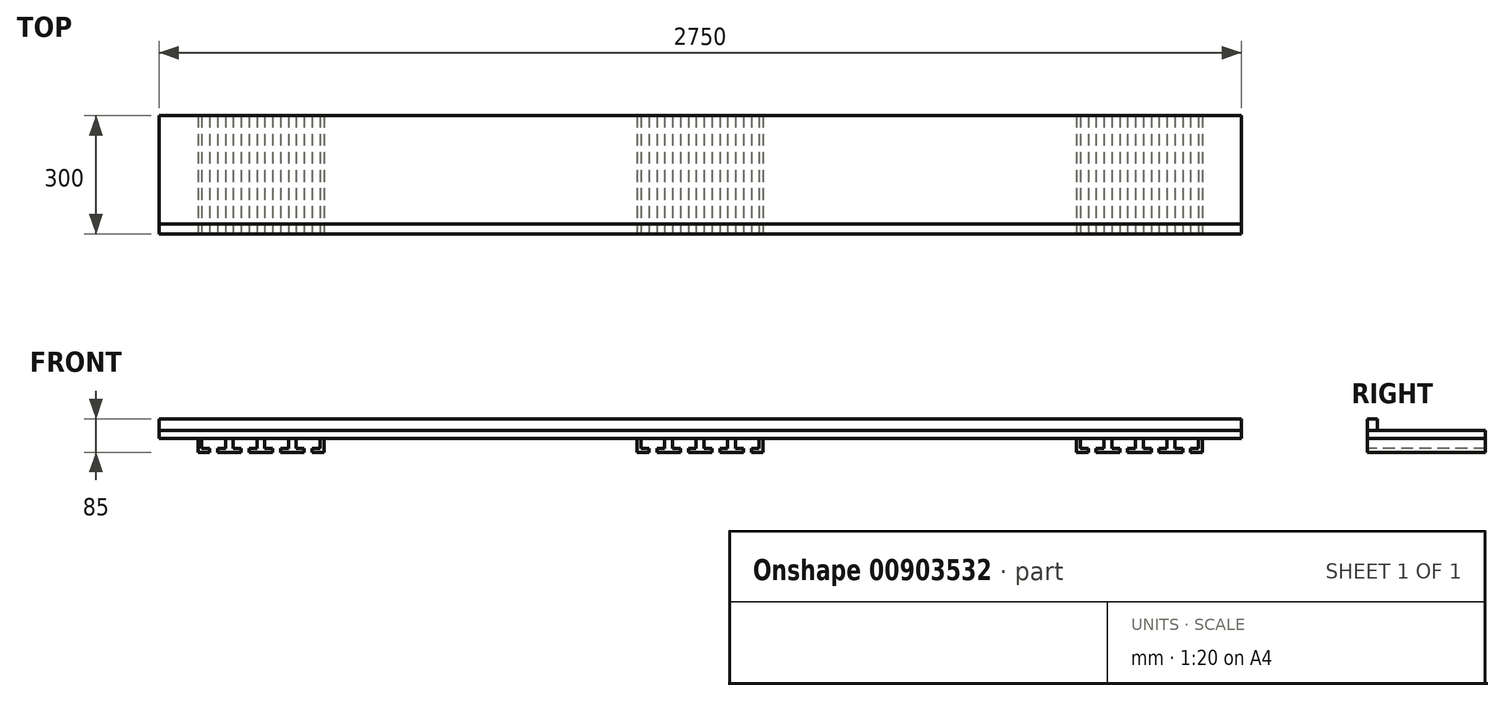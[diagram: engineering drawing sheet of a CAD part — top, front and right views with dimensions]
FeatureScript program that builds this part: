
annotation { "Feature Type Name" : "Feature", "Feature Type Description" : "" }
export const myFeature = defineFeature(function(context is Context, id is Id, definition is map)
    precondition{}
    {
        {
            var Q0;
            Q0=qCreatedBy(makeId("Front.planeOp"),FACE);
            var sketch = newSketch(context, id + "F0", { "sketchPlane" : qUnion([Q0])});
            skLineSegment(sketch, "E0.bottom", {"start": v(1375, -10) * mm, "end": v(-1375, -10) * mm});
            skLineSegment(sketch, "E0.top", {"start": v(1375, 10) * mm, "end": v(-1375, 10) * mm});
            skLineSegment(sketch, "E0.left", {"start": v(1375, -10) * mm, "end": v(1375, 10) * mm});
            skLineSegment(sketch, "E0.right", {"start": v(-1375, -10) * mm, "end": v(-1375, 10) * mm});
            skPoint(sketch, "E0.middle", {"position": v(0, 0) * mm});
            skSolve(sketch);
        }
        {
            var Q0;
            Q0 = qSketchRegion(id + "F0", true);
            extrude(context, id + "F1", {"entities" : qUnion([Q0]), "depth" : 300 * mm, "offsetDistance" : 25 * mm});
        }
        {
            var Q0;
            Q0=makeQuery(id+"F1.opExtrude","SWEPT_FACE",FACE,{"disambiguationData":[OSD([sQuery(id+"F0.wireOp",EDGE,"E0.top")])]});
            var sketch = newSketch(context, id + "F2", { "sketchPlane" : qUnion([Q0])});
            skLineSegment(sketch, "E1.bottom", {"start": v(-1375, -300) * mm, "end": v(1375, -300) * mm});
            skLineSegment(sketch, "E1.top", {"start": v(-1375, -275) * mm, "end": v(1375, -275) * mm});
            skLineSegment(sketch, "E1.left", {"start": v(-1375, -300) * mm, "end": v(-1375, -275) * mm});
            skLineSegment(sketch, "E1.right", {"start": v(1375, -300) * mm, "end": v(1375, -275) * mm});
            skSolve(sketch);
        }
        {
            var Q0;
            Q0 = qSketchRegion(id + "F2", true);
            extrude(context, id + "F3", {"entities" : qUnion([Q0]), "depth" : 30 * mm, "offsetDistance" : 25 * mm});
        }
        {
            var Q0;
            Q0=makeQuery(id+"F1.opExtrude","CAP_FACE",FACE,{"disambiguationData":[OSD([sQuery(id+"F0.wireOp",EDGE,"E0.bottom"),sQuery(id+"F0.wireOp",EDGE,"E0.top"),sQuery(id+"F0.wireOp",EDGE,"E0.left"),sQuery(id+"F0.wireOp",EDGE,"E0.right")])],"isStart":false});
            var sketch = newSketch(context, id + "F4", { "sketchPlane" : qUnion([Q0])});
            skLineSegment(sketch, "E2", {"start": v(0, 0) * mm, "end": v(0, -360.98) * mm, "construction": true});
            skLineSegment(sketch, "E3", {"start": v(0, 0) * mm, "end": v(0, -45) * mm});
            skLineSegment(sketch, "E4", {"start": v(0, -45) * mm, "end": v(30, -45) * mm});
            skLineSegment(sketch, "E5", {"start": v(30, -45) * mm, "end": v(30, -35) * mm});
            skLineSegment(sketch, "E6", {"start": v(30, -35) * mm, "end": v(10, -35) * mm});
            skLineSegment(sketch, "E7", {"start": v(10, -35) * mm, "end": v(10, -10) * mm});
            skLineSegment(sketch, "E8", {"start": v(10, -10) * mm, "end": v(0, -10) * mm});
            skLineSegment(sketch, "E9.MirrorCS", {"start": v(-10, -10) * mm, "end": v(0, -10) * mm});
            skLineSegment(sketch, "E10.MirrorCS", {"start": v(-10, -35) * mm, "end": v(-10, -10) * mm});
            skLineSegment(sketch, "E11.MirrorCS", {"start": v(-30, -35) * mm, "end": v(-10, -35) * mm});
            skLineSegment(sketch, "E12.MirrorCS", {"start": v(-30, -45) * mm, "end": v(-30, -35) * mm});
            skLineSegment(sketch, "E13.MirrorCS", {"start": v(0, -45) * mm, "end": v(-30, -45) * mm});
            skLineSegment(sketch, "E14", {"start": v(40, -10) * mm, "end": v(40, -247.73) * mm, "construction": true});
            skLineSegment(sketch, "E15.MirrorCS", {"start": v(80, -45) * mm, "end": v(50, -45) * mm});
            skLineSegment(sketch, "E16.MirrorCS", {"start": v(50, -45) * mm, "end": v(50, -35) * mm});
            skLineSegment(sketch, "E17.MirrorCS", {"start": v(50, -35) * mm, "end": v(70, -35) * mm});
            skLineSegment(sketch, "E18.MirrorCS", {"start": v(70, -35) * mm, "end": v(70, -10) * mm});
            skLineSegment(sketch, "E19.MirrorCS", {"start": v(70, -10) * mm, "end": v(80, -10) * mm});
            skLineSegment(sketch, "E20", {"start": v(80, -10) * mm, "end": v(80, -45) * mm});
            skLineSegment(sketch, "E21.MirrorCS", {"start": v(-80, -10) * mm, "end": v(-80, -45) * mm});
            skLineSegment(sketch, "E22.MirrorCS", {"start": v(-70, -10) * mm, "end": v(-80, -10) * mm});
            skLineSegment(sketch, "E23.MirrorCS", {"start": v(-70, -35) * mm, "end": v(-70, -10) * mm});
            skLineSegment(sketch, "E24.MirrorCS", {"start": v(-50, -35) * mm, "end": v(-70, -35) * mm});
            skLineSegment(sketch, "E25.MirrorCS", {"start": v(-50, -45) * mm, "end": v(-50, -35) * mm});
            skLineSegment(sketch, "E26.MirrorCS", {"start": v(-80, -45) * mm, "end": v(-50, -45) * mm});
            skLineSegment(sketch, "E27.MirrorCS", {"start": v(90, -10) * mm, "end": v(80, -10) * mm});
            skLineSegment(sketch, "E28.MirrorCS", {"start": v(90, -35) * mm, "end": v(90, -10) * mm});
            skLineSegment(sketch, "E29.MirrorCS", {"start": v(110, -35) * mm, "end": v(90, -35) * mm});
            skLineSegment(sketch, "E30.MirrorCS", {"start": v(110, -45) * mm, "end": v(110, -35) * mm});
            skLineSegment(sketch, "E31.MirrorCS", {"start": v(80, -45) * mm, "end": v(110, -45) * mm});
            skLineSegment(sketch, "E32.MirrorCS", {"start": v(120, -10) * mm, "end": v(120, -247.73) * mm, "construction": true});
            skLineSegment(sketch, "E33.MirrorCS", {"start": v(160, -45) * mm, "end": v(130, -45) * mm});
            skLineSegment(sketch, "E34.MirrorCS", {"start": v(160, -10) * mm, "end": v(160, -45) * mm});
            skLineSegment(sketch, "E35.MirrorCS", {"start": v(150, -10) * mm, "end": v(160, -10) * mm});
            skLineSegment(sketch, "E36.MirrorCS", {"start": v(150, -35) * mm, "end": v(150, -10) * mm});
            skLineSegment(sketch, "E37.MirrorCS", {"start": v(130, -35) * mm, "end": v(150, -35) * mm});
            skLineSegment(sketch, "E38.MirrorCS", {"start": v(130, -45) * mm, "end": v(130, -35) * mm});
            skLineSegment(sketch, "E39.MirrorCS", {"start": v(-150, -10) * mm, "end": v(-160, -10) * mm});
            skLineSegment(sketch, "E40.MirrorCS", {"start": v(-160, -45) * mm, "end": v(-130, -45) * mm});
            skLineSegment(sketch, "E41.MirrorCS", {"start": v(-160, -10) * mm, "end": v(-160, -45) * mm});
            skLineSegment(sketch, "E42.MirrorCS", {"start": v(-150, -35) * mm, "end": v(-150, -10) * mm});
            skLineSegment(sketch, "E43.MirrorCS", {"start": v(-130, -45) * mm, "end": v(-130, -35) * mm});
            skLineSegment(sketch, "E44.MirrorCS", {"start": v(-130, -35) * mm, "end": v(-150, -35) * mm});
            skLineSegment(sketch, "E45.MirrorCS", {"start": v(-110, -45) * mm, "end": v(-110, -35) * mm});
            skLineSegment(sketch, "E46.MirrorCS", {"start": v(-110, -35) * mm, "end": v(-90, -35) * mm});
            skLineSegment(sketch, "E47.MirrorCS", {"start": v(-80, -45) * mm, "end": v(-110, -45) * mm});
            skLineSegment(sketch, "E48.MirrorCS", {"start": v(-90, -35) * mm, "end": v(-90, -10) * mm});
            skLineSegment(sketch, "E49.MirrorCS", {"start": v(-90, -10) * mm, "end": v(-80, -10) * mm});
            skSolve(sketch);
        }
        {
            var Q0;
            Q0 = qSketchRegion(id + "F4", true);
            extrude(context, id + "F5", {"entities" : qUnion([Q0]), "oppositeDirection" : true, "depth" : 300 * mm, "offsetDistance" : 25 * mm});
        }
        {
            var Q0;
            Q0=makeQuery(id+"F1.opExtrude","SWEPT_FACE",FACE,{"disambiguationData":[OSD([sQuery(id+"F0.wireOp",EDGE,"E0.left")])]});
            cPlane(context, id + "F6", {"entities" : qUnion([Q0]), "cplaneType" : CPlaneType.OFFSET, "offset" : 817 * mm, "oppositeDirection" : true, "width" : 150 * mm, "height" : 150 * mm});
        }
        {
            var Q0;
            Q0=makeQuery(id+"F5.opExtrude","SWEPT_BODY",BODY,{"disambiguationData":[OSD([sQuery(id+"F4.wireOp",EDGE,"E4"),sQuery(id+"F4.wireOp",EDGE,"E5"),sQuery(id+"F4.wireOp",EDGE,"E6"),sQuery(id+"F4.wireOp",EDGE,"E7"),sQuery(id+"F4.wireOp",EDGE,"E8"),sQuery(id+"F4.wireOp",EDGE,"E9.MirrorCS"),sQuery(id+"F4.wireOp",EDGE,"E10.MirrorCS"),sQuery(id+"F4.wireOp",EDGE,"E11.MirrorCS"),sQuery(id+"F4.wireOp",EDGE,"E12.MirrorCS"),sQuery(id+"F4.wireOp",EDGE,"E13.MirrorCS")])]});
            var Q1;
            Q1=makeQuery(id+"F5.opExtrude","SWEPT_BODY",BODY,{"disambiguationData":[OSD([sQuery(id+"F4.wireOp",EDGE,"E33.MirrorCS"),sQuery(id+"F4.wireOp",EDGE,"E34.MirrorCS"),sQuery(id+"F4.wireOp",EDGE,"E35.MirrorCS"),sQuery(id+"F4.wireOp",EDGE,"E36.MirrorCS"),sQuery(id+"F4.wireOp",EDGE,"E37.MirrorCS"),sQuery(id+"F4.wireOp",EDGE,"E38.MirrorCS")])]});
            var Q2;
            Q2=makeQuery(id+"F5.opExtrude","SWEPT_BODY",BODY,{"disambiguationData":[OSD([sQuery(id+"F4.wireOp",EDGE,"E22.MirrorCS"),sQuery(id+"F4.wireOp",EDGE,"E23.MirrorCS"),sQuery(id+"F4.wireOp",EDGE,"E24.MirrorCS"),sQuery(id+"F4.wireOp",EDGE,"E25.MirrorCS"),sQuery(id+"F4.wireOp",EDGE,"E26.MirrorCS"),sQuery(id+"F4.wireOp",EDGE,"E45.MirrorCS"),sQuery(id+"F4.wireOp",EDGE,"E46.MirrorCS"),sQuery(id+"F4.wireOp",EDGE,"E47.MirrorCS"),sQuery(id+"F4.wireOp",EDGE,"E48.MirrorCS"),sQuery(id+"F4.wireOp",EDGE,"E49.MirrorCS")])]});
            var Q3;
            Q3=makeQuery(id+"F5.opExtrude","SWEPT_BODY",BODY,{"disambiguationData":[OSD([sQuery(id+"F4.wireOp",EDGE,"E15.MirrorCS"),sQuery(id+"F4.wireOp",EDGE,"E16.MirrorCS"),sQuery(id+"F4.wireOp",EDGE,"E17.MirrorCS"),sQuery(id+"F4.wireOp",EDGE,"E18.MirrorCS"),sQuery(id+"F4.wireOp",EDGE,"E19.MirrorCS"),sQuery(id+"F4.wireOp",EDGE,"E27.MirrorCS"),sQuery(id+"F4.wireOp",EDGE,"E28.MirrorCS"),sQuery(id+"F4.wireOp",EDGE,"E29.MirrorCS"),sQuery(id+"F4.wireOp",EDGE,"E30.MirrorCS"),sQuery(id+"F4.wireOp",EDGE,"E31.MirrorCS")])]});
            var Q4;
            Q4=makeQuery(id+"F5.opExtrude","SWEPT_BODY",BODY,{"disambiguationData":[OSD([sQuery(id+"F4.wireOp",EDGE,"E39.MirrorCS"),sQuery(id+"F4.wireOp",EDGE,"E40.MirrorCS"),sQuery(id+"F4.wireOp",EDGE,"E41.MirrorCS"),sQuery(id+"F4.wireOp",EDGE,"E42.MirrorCS"),sQuery(id+"F4.wireOp",EDGE,"E43.MirrorCS"),sQuery(id+"F4.wireOp",EDGE,"E44.MirrorCS")])]});
            var Q5;
            Q5=qCreatedBy(id+"F6.planeOp",FACE);
            mirror(context, id + "F7", {"entities" : qUnion([Q0, Q1, Q2, Q3, Q4]), "mirrorPlane" : qUnion([Q5])});
        }
        {
            var Q0;
            Q0=makeQuery(id+"F7.opPattern","COPY",BODY,{"derivedFrom":makeQuery(id+"F5.opExtrude","SWEPT_BODY",BODY,{"disambiguationData":[OSD([sQuery(id+"F4.wireOp",EDGE,"E33.MirrorCS"),sQuery(id+"F4.wireOp",EDGE,"E34.MirrorCS"),sQuery(id+"F4.wireOp",EDGE,"E35.MirrorCS"),sQuery(id+"F4.wireOp",EDGE,"E36.MirrorCS"),sQuery(id+"F4.wireOp",EDGE,"E37.MirrorCS"),sQuery(id+"F4.wireOp",EDGE,"E38.MirrorCS")])]}),"instanceName":"1"});
            var Q1;
            Q1=makeQuery(id+"F7.opPattern","COPY",BODY,{"derivedFrom":makeQuery(id+"F5.opExtrude","SWEPT_BODY",BODY,{"disambiguationData":[OSD([sQuery(id+"F4.wireOp",EDGE,"E15.MirrorCS"),sQuery(id+"F4.wireOp",EDGE,"E16.MirrorCS"),sQuery(id+"F4.wireOp",EDGE,"E17.MirrorCS"),sQuery(id+"F4.wireOp",EDGE,"E18.MirrorCS"),sQuery(id+"F4.wireOp",EDGE,"E19.MirrorCS"),sQuery(id+"F4.wireOp",EDGE,"E27.MirrorCS"),sQuery(id+"F4.wireOp",EDGE,"E28.MirrorCS"),sQuery(id+"F4.wireOp",EDGE,"E29.MirrorCS"),sQuery(id+"F4.wireOp",EDGE,"E30.MirrorCS"),sQuery(id+"F4.wireOp",EDGE,"E31.MirrorCS")])]}),"instanceName":"1"});
            var Q2;
            Q2=makeQuery(id+"F7.opPattern","COPY",BODY,{"derivedFrom":makeQuery(id+"F5.opExtrude","SWEPT_BODY",BODY,{"disambiguationData":[OSD([sQuery(id+"F4.wireOp",EDGE,"E4"),sQuery(id+"F4.wireOp",EDGE,"E5"),sQuery(id+"F4.wireOp",EDGE,"E6"),sQuery(id+"F4.wireOp",EDGE,"E7"),sQuery(id+"F4.wireOp",EDGE,"E8"),sQuery(id+"F4.wireOp",EDGE,"E9.MirrorCS"),sQuery(id+"F4.wireOp",EDGE,"E10.MirrorCS"),sQuery(id+"F4.wireOp",EDGE,"E11.MirrorCS"),sQuery(id+"F4.wireOp",EDGE,"E12.MirrorCS"),sQuery(id+"F4.wireOp",EDGE,"E13.MirrorCS")])]}),"instanceName":"1"});
            var Q3;
            Q3=makeQuery(id+"F7.opPattern","COPY",BODY,{"derivedFrom":makeQuery(id+"F5.opExtrude","SWEPT_BODY",BODY,{"disambiguationData":[OSD([sQuery(id+"F4.wireOp",EDGE,"E22.MirrorCS"),sQuery(id+"F4.wireOp",EDGE,"E23.MirrorCS"),sQuery(id+"F4.wireOp",EDGE,"E24.MirrorCS"),sQuery(id+"F4.wireOp",EDGE,"E25.MirrorCS"),sQuery(id+"F4.wireOp",EDGE,"E26.MirrorCS"),sQuery(id+"F4.wireOp",EDGE,"E45.MirrorCS"),sQuery(id+"F4.wireOp",EDGE,"E46.MirrorCS"),sQuery(id+"F4.wireOp",EDGE,"E47.MirrorCS"),sQuery(id+"F4.wireOp",EDGE,"E48.MirrorCS"),sQuery(id+"F4.wireOp",EDGE,"E49.MirrorCS")])]}),"instanceName":"1"});
            var Q4;
            Q4=makeQuery(id+"F7.opPattern","COPY",BODY,{"derivedFrom":makeQuery(id+"F5.opExtrude","SWEPT_BODY",BODY,{"disambiguationData":[OSD([sQuery(id+"F4.wireOp",EDGE,"E39.MirrorCS"),sQuery(id+"F4.wireOp",EDGE,"E40.MirrorCS"),sQuery(id+"F4.wireOp",EDGE,"E41.MirrorCS"),sQuery(id+"F4.wireOp",EDGE,"E42.MirrorCS"),sQuery(id+"F4.wireOp",EDGE,"E43.MirrorCS"),sQuery(id+"F4.wireOp",EDGE,"E44.MirrorCS")])]}),"instanceName":"1"});
            var Q5;
            Q5=qCreatedBy(makeId("Right.planeOp"),FACE);
            mirror(context, id + "F8", {"entities" : qUnion([Q0, Q1, Q2, Q3, Q4]), "mirrorPlane" : qUnion([Q5])});
        }
    });
